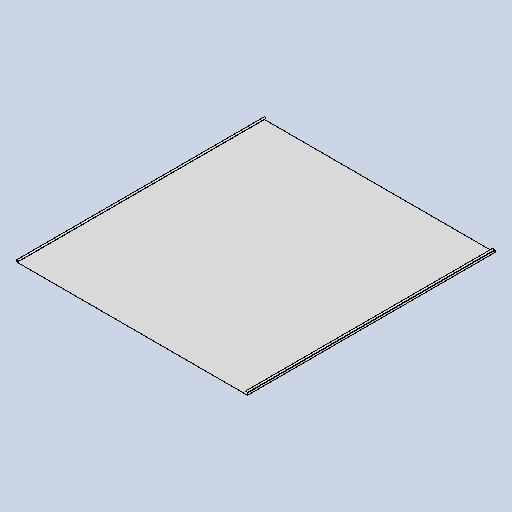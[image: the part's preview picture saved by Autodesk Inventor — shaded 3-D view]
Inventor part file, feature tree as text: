
AUTODESK INVENTOR PART (.ipt)
format: ipt  version: 2025 (Build 290162010, 162A)  size: 194,560 bytes
history: native  units: mm
features: sheet_metal_op x7, sketch x4, other x4, extrude x1, chamfer x1, projected_geometry x1
ambient origin geometry x8: Origin, YZ Plane, XZ Plane, XY Plane, X Axis, Y Axis, Z Axis, Center Point
bodies: Body1 (feature_tree)
feature tree (18):
  sheet_metal_op  "Face1"
  sheet_metal_op  "Flange1"
  sheet_metal_op  "Flange2"
  extrude  "Extrusion3"  Depth=915.0mm
  chamfer  "Corner Round1"
  sketch  "Sketch6"  dims[d12=23.212879mm d52=915.0mm]
  other  "Plate2"
  sketch  "Sketch10"  dims[d53=980.0mm]
  other  "Plate3"
  sheet_metal_op  "Bend2"
  sheet_metal_op  "Corner2"
  sketch  "Sketch11"  dims[d54=0.5mm]
  other  "Plate4"
  sheet_metal_op  "Bend3"
  sheet_metal_op  "Corner3"
  sketch  "Sketch12"  dims[d74=0.5mm d75=0.25mm d76=1.0mm d77=0.5mm d78=10.0mm d79=90.0deg d80=0.5mm d81=2.0mm d82=0.5mm d83=0.5mm d84=0.5mm d85=0.25mm d86=1.0mm d87=0.5mm d88=10.0mm d89=90.0deg d90=0.5mm d91=2.0mm d92=0.5mm d93=0.5mm d94=0.0mm d95=0.0mm d96=100.0mm d97=40.0mm d98=100.0mm d99=40.0mm d100=4.0mm]
  projected_geometry  "Projected Loop5"
  other  "Definition1"
